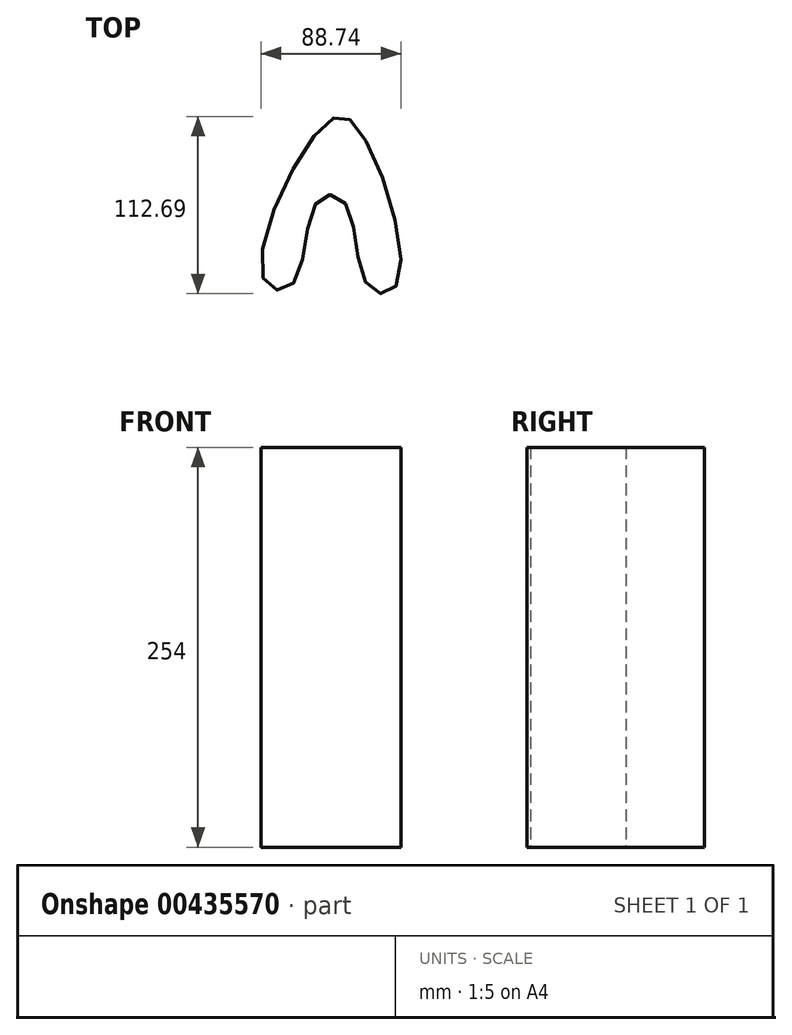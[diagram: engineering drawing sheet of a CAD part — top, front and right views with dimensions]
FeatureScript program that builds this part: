
annotation { "Feature Type Name" : "Feature", "Feature Type Description" : "" }
export const myFeature = defineFeature(function(context is Context, id is Id, definition is map)
    precondition{}
    {
        {
            var Q0;
            Q0=qCreatedBy(makeId("Top.planeOp"),FACE);
            var sketch = newSketch(context, id + "F0", { "sketchPlane" : qUnion([Q0])});
            skFitSpline(sketch, "E0", {"points": [v(-46.05, -44.32) * mm, v(-7.77, 52.67) * mm, v(14.1, 50.94) * mm, v(38.85, -48.64) * mm, v(20.72, -49.5) * mm, v(6.04, 3.17) * mm, v(-11.8, 4.32) * mm, v(-27.63, -48.64) * mm, v(-46.05, -44.32) * mm]});
            skSolve(sketch);
        }
        {
            var Q0;
            Q0 = qSketchRegion(id + "F0", true);
            extrude(context, id + "F1", {"entities" : qUnion([Q0]), "depth" : 254 * mm});
        }
    });
